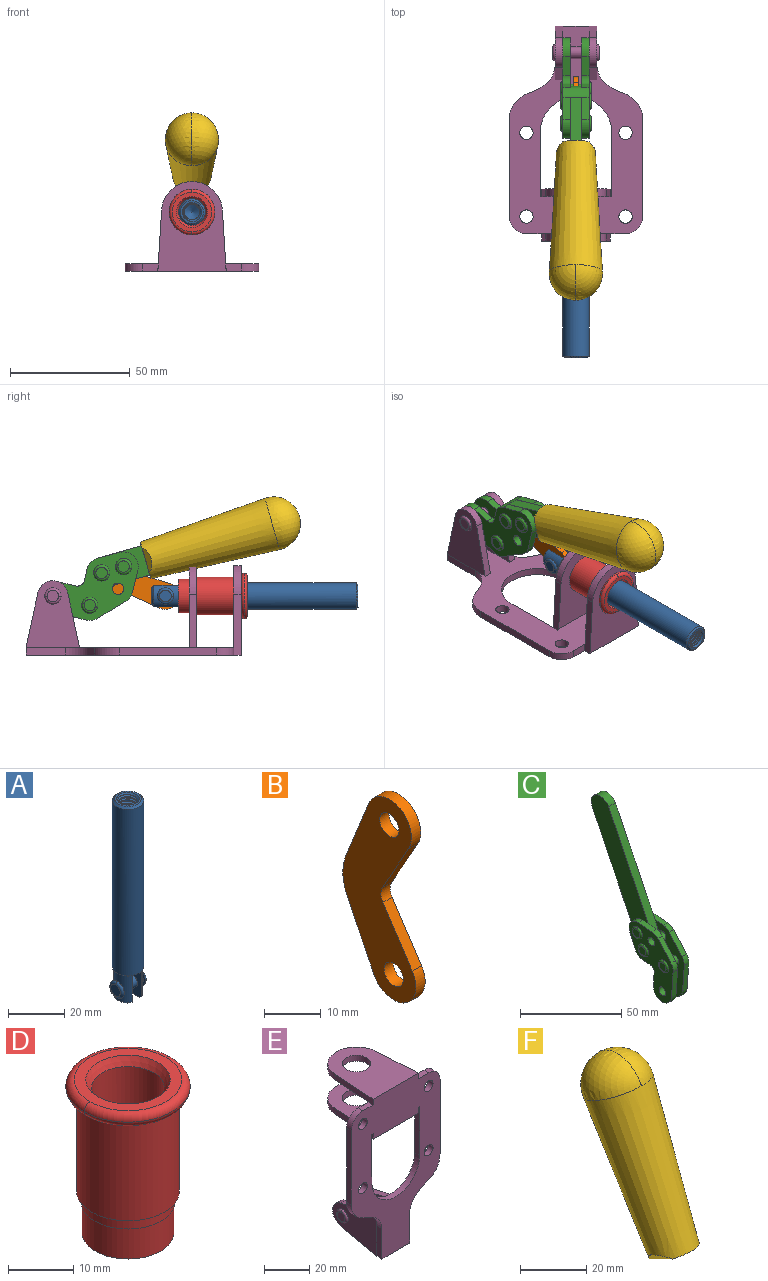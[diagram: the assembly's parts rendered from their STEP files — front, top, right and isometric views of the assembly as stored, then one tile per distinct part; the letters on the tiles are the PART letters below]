
ASSEMBLY  parts=6 mates=6
PART A: 48 faces, bbox 12.6x11.1x86.1 mm
  f0: torus R=2.41mm, axis (-1,0,0), area 15mm2, adj f30,f32,f34
  f1: torus R=2.41mm, axis (-1,0,0), area 15mm2, adj f29,f31,f33
  f2: cylinder r=5.54mm len=72.39mm, axis (0,0,1), area 2518.5mm2, adj f3,f4,f42,f43
  f3: cone r=5.54mm half-angle=45deg, axis (0,0,1), area 7.6mm2, adj f2,f5,f41
  f4: cone r=5.54mm half-angle=45deg, axis (0,0,-1), area 34.9mm2, adj f2,f39
  f5: cylinder r=5.08mm len=11.48mm, axis (0,0,1), area 108.3mm2, adj f3,f7,f8,f41
  f6: cylinder r=2.41mm len=4.83mm, axis (-1,0,0), area 71.2mm2, adj f40,f41
  f7: cylinder r=2.41mm len=4.83mm, axis (-1,0,0), area 7.6mm2, adj f5,f34
  f8: cone r=5.08mm half-angle=45deg, axis (0,0,1), area 10.6mm2, adj f5,f37,f41
  f9: cone r=3.98mm half-angle=45deg, axis (0,0,1), area 17.6mm2, adj f27,f39,f45,f46,f47
  f10: cylinder r=2.41mm len=4.83mm, axis (-1,0,0), area 7.6mm2, adj f33,f38
  f11: cylinder r=3.2mm len=6.4mm, axis (0,0,1), area 78.4mm2, adj f12,f28,f44,f45,f47
  f12: cylinder r=3.2mm len=6.4mm, axis (0,0,1), area 10.5mm2, adj f11,f13,f45,f47
  f13: cylinder r=3.2mm len=6.4mm, axis (0,0,1), area 10.5mm2, adj f12,f14,f45,f47
  f14: cylinder r=3.2mm len=6.4mm, axis (0,0,1), area 10.5mm2, adj f13,f15,f45,f47
  f15: cylinder r=3.2mm len=6.4mm, axis (0,0,1), area 10.5mm2, adj f14,f16,f45,f47
  f16: cylinder r=3.2mm len=6.4mm, axis (0,0,1), area 10.5mm2, adj f15,f17,f45,f47
  f17: cylinder r=3.2mm len=6.4mm, axis (0,0,1), area 10.5mm2, adj f16,f18,f45,f47
  f18: cylinder r=3.2mm len=6.4mm, axis (0,0,1), area 10.5mm2, adj f17,f19,f45,f47
  f19: cylinder r=3.2mm len=6.4mm, axis (0,0,1), area 10.5mm2, adj f18,f20,f45,f47
  f20: cylinder r=3.2mm len=6.4mm, axis (0,0,1), area 10.5mm2, adj f19,f21,f45,f47
  f21: cylinder r=3.2mm len=6.4mm, axis (0,0,1), area 10.5mm2, adj f20,f22,f45,f47
  f22: cylinder r=3.2mm len=6.4mm, axis (0,0,1), area 10.5mm2, adj f21,f23,f45,f47
  f23: cylinder r=3.2mm len=6.4mm, axis (0,0,1), area 10.5mm2, adj f22,f24,f45,f47
  f24: cylinder r=3.2mm len=6.4mm, axis (0,0,1), area 10.5mm2, adj f23,f25,f45,f47
  f25: cylinder r=3.2mm len=6.4mm, axis (0,0,1), area 10.5mm2, adj f24,f26,f45,f47
  f26: cylinder r=3.2mm len=6.4mm, axis (0,0,1), area 10.5mm2, adj f25,f27,f45,f47
  f27: cylinder r=3.2mm len=6.4mm, axis (0,0,1), area 7.4mm2, adj f9,f26,f45,f47
  f28: cone r=3.2mm half-angle=60deg, axis (0,0,1), area 37.2mm2, adj f11
  f29: plane 4.83x4.83mm, normal (-1,0,0), area 18.3mm2, adj f1,f31
  f30: plane 4.83x4.83mm, normal (1,0,0), area 18.3mm2, adj f0,f32
  f31: torus R=2.41mm, axis (-1,0,0), area 15mm2, adj f1,f29,f33
  f32: torus R=2.41mm, axis (-1,0,0), area 15mm2, adj f0,f30,f34
  f33: plane 6.83x6.83mm, normal (1,0,0), area 18.3mm2, adj f1,f10,f31
  f34: plane 6.83x6.83mm, normal (-1,0,0), area 18.3mm2, adj f0,f7,f32
  f35: cone r=5.08mm half-angle=45deg, axis (0,0,1), area 10.6mm2, adj f36,f38,f40
  f36: plane 7.25x1.97mm, normal (0,0,-1), area 10mm2, adj f35,f40
  f37: plane 7.25x1.97mm, normal (0,0,-1), area 10mm2, adj f8,f41
  f38: cylinder r=5.08mm len=11.48mm, axis (0,0,1), area 108.3mm2, adj f10,f35,f40,f42
  f39: plane 9.55x9.55mm, normal (0,0,1), area 22mm2, adj f4,f9
  f40: plane 12.76x10.09mm, normal (1,0,0), area 95.7mm2, adj f6,f35,f36,f38,f42,f43
  f41: plane 12.76x10.09mm, normal (-1,0,0), area 95.7mm2, adj f3,f5,f6,f8,f37,f43
  f42: cone r=5.54mm half-angle=45deg, axis (0,0,1), area 7.6mm2, adj f2,f38,f40
  f43: plane 11.07x4.7mm, normal (0,0,-1), area 50.4mm2, adj f2,f40,f41
  f44: plane 0.89x0.62mm, normal (-1,0,0), area 0.3mm2, adj f11,f45,f46,f47
  f45: bspline ~24.8x7.63mm, area 266.6mm2, adj f9,f11,f12,f13,f14,f15,f16,f17
  f46: bspline ~24.87x7.63mm, area 73.6mm2, adj f9,f44,f45,f47
  f47: bspline ~24.98x7.63mm, area 272.5mm2, adj f9,f11,f12,f13,f14,f15,f16,f17
PART B: 12 faces, bbox 2.3x18.2x42.8 mm
  f0: cylinder r=2.4mm len=4.8mm, axis (1,0,0), area 34.9mm2, adj f4,f11
  f1: cylinder r=10.41mm len=8.47mm, axis (1,0,0), area 20.2mm2, adj f4,f9,f10,f11
  f2: cylinder r=3.05mm len=3.16mm, axis (1,0,0), area 7.7mm2, adj f4,f6,f7,f11
  f3: cylinder r=2.4mm len=4.8mm, axis (1,0,0), area 34.9mm2, adj f4,f11
  f4: plane 42.81x18.23mm, normal (-1,0,0), area 414.1mm2, adj f0,f1,f2,f3,f5,f6,f7,f8
  f5: cylinder r=5.54mm len=10.67mm, axis (1,0,0), area 41.8mm2, adj f4,f6,f10,f11
  f6: plane 11.66x6.53mm, normal (0,-0.87,-0.49), area 30.9mm2, adj f2,f4,f5,f11
  f7: plane 11.17x7.33mm, normal (0,-0.84,0.55), area 30.9mm2, adj f2,f4,f8,f11
  f8: cylinder r=5.54mm len=10.51mm, axis (1,0,0), area 41.8mm2, adj f4,f7,f9,f11
  f9: plane 13.67x6.67mm, normal (0,0.9,-0.44), area 35.1mm2, adj f1,f4,f8,f11
  f10: plane 14.1x5.7mm, normal (0,0.93,0.37), area 35.1mm2, adj f1,f4,f5,f11
  f11: plane 42.81x18.23mm, normal (1,0,0), area 414.1mm2, adj f0,f1,f2,f3,f5,f6,f7,f8
PART C: 59 faces, bbox 12.9x60.2x99.6 mm
  f0: torus R=2.39mm, axis (-1,0,0), area 14.9mm2, adj f20,f43,f51
  f1: torus R=2.39mm, axis (-1,0,0), area 14.9mm2, adj f19,f42,f51
  f2: torus R=2.39mm, axis (-1,0,0), area 14.9mm2, adj f18,f35,f51
  f3: torus R=2.39mm, axis (-1,0,0), area 14.9mm2, adj f14,f17,f23
  f4: torus R=2.39mm, axis (-1,0,0), area 14.9mm2, adj f13,f16,f23
  f5: torus R=2.39mm, axis (-1,0,0), area 14.9mm2, adj f12,f15,f23
  f6: cylinder r=2.39mm len=4.78mm, axis (1,0,0), area 46.5mm2, adj f48,f50,f51
  f7: cylinder r=2.39mm len=4.78mm, axis (1,0,0), area 46.5mm2, adj f50,f51
  f8: cylinder r=6.35mm len=12.68mm, axis (1,0,0), area 61.8mm2, adj f38,f39,f50,f51
  f9: cylinder r=2.39mm len=4.78mm, axis (-1,0,0), area 70.5mm2, adj f46,f50
  f10: cylinder r=2.39mm len=4.78mm, axis (-1,0,0), area 46.5mm2, adj f23,f45,f46
  f11: cylinder r=2.39mm len=4.78mm, axis (-1,0,0), area 46.5mm2, adj f23,f46
  f12: plane 4.78x4.78mm, normal (1,0,0), area 17.9mm2, adj f5,f15
  f13: plane 4.78x4.78mm, normal (1,0,0), area 17.9mm2, adj f4,f16
  f14: plane 4.78x4.78mm, normal (1,0,0), area 17.9mm2, adj f3,f17
  f15: torus R=2.39mm, axis (-1,0,0), area 14.9mm2, adj f5,f12,f23
  f16: torus R=2.39mm, axis (-1,0,0), area 14.9mm2, adj f4,f13,f23
  f17: torus R=2.39mm, axis (-1,0,0), area 14.9mm2, adj f3,f14,f23
  f18: plane 4.78x4.78mm, normal (-1,0,0), area 17.9mm2, adj f2,f35
  f19: plane 4.78x4.78mm, normal (-1,0,0), area 17.9mm2, adj f1,f42
  f20: plane 4.78x4.78mm, normal (-1,0,0), area 17.9mm2, adj f0,f43
  f21: plane 2.26x0.2mm, normal (1,0,0), area 0.2mm2, adj f31,f44
  f22: plane 2.26x0.2mm, normal (-1,0,0), area 0.2mm2, adj f41,f44
  f23: plane 39.37x30.77mm, normal (1,0,0), area 565.5mm2, adj f3,f4,f5,f10,f11,f15,f16,f17
  f24: cylinder r=6.1mm len=4.15mm, axis (-1,0,0), area 14.7mm2, adj f23,f25,f32,f46
  f25: plane 10.25x9.01mm, normal (0,-0.75,0.66), area 42.3mm2, adj f23,f24,f26,f46
  f26: cylinder r=6.35mm len=4.64mm, axis (-1,0,0), area 15.6mm2, adj f23,f25,f27,f46
  f27: plane 15.84x3.1mm, normal (0,-1,-0.07), area 49.2mm2, adj f23,f26,f28,f46
  f28: cylinder r=6.35mm len=12.68mm, axis (-1,0,0), area 61.8mm2, adj f23,f27,f29,f46
  f29: plane 8.11x3.1mm, normal (0,1,0.07), area 25.2mm2, adj f23,f28,f30,f46
  f30: cylinder r=3.05mm len=3.25mm, axis (-1,0,0), area 14.8mm2, adj f23,f29,f31,f46
  f31: plane 5.99x3.1mm, normal (0,0.07,-1), area 18.6mm2, adj f21,f23,f30,f44,f46
  f32: plane 9.5x3.1mm, normal (0,-0.07,1), area 29.5mm2, adj f23,f24,f33,f46,f47
  f33: cylinder r=6.1mm len=8.63mm, axis (-1,0,0), area 39.1mm2, adj f23,f32,f34,f47
  f34: plane 8.65x3.96mm, normal (0,0.91,-0.42), area 29.5mm2, adj f23,f33,f44,f47
  f35: torus R=2.39mm, axis (-1,0,0), area 14.9mm2, adj f2,f18,f51
  f36: plane 10.25x9.01mm, normal (0,-0.75,0.66), area 42.3mm2, adj f37,f49,f50,f51
  f37: cylinder r=6.35mm len=4.64mm, axis (1,0,0), area 15.6mm2, adj f36,f38,f50,f51
  f38: plane 15.84x3.1mm, normal (0,-1,-0.07), area 49.2mm2, adj f8,f37,f50,f51
  f39: plane 8.11x3.1mm, normal (0,1,0.07), area 25.2mm2, adj f8,f40,f50,f51
  f40: cylinder r=3.05mm len=3.25mm, axis (1,0,0), area 14.8mm2, adj f39,f41,f50,f51
  f41: plane 5.99x3.1mm, normal (0,0.07,-1), area 18.6mm2, adj f22,f40,f44,f50,f51
  f42: torus R=2.39mm, axis (-1,0,0), area 14.9mm2, adj f1,f19,f51
  f43: torus R=2.39mm, axis (-1,0,0), area 14.9mm2, adj f0,f20,f51
  f44: cylinder r=6.35mm len=12.12mm, axis (-1,0,0), area 128.9mm2, adj f21,f22,f23,f31,f34,f41,f46,f47
  f45: plane 2.65x1.35mm, normal (1,0,0), area 1mm2, adj f10,f55
  f46: plane 39.08x20.42mm, normal (-1,0,0), area 412.5mm2, adj f9,f10,f11,f24,f25,f26,f27,f28
  f47: plane 77.62x39.82mm, normal (1,0,0), area 850mm2, adj f32,f33,f34,f44,f53,f54,f55
  f48: plane 2.65x1.35mm, normal (-1,0,0), area 1mm2, adj f6,f55
  f49: cylinder r=6.1mm len=4.15mm, axis (1,0,0), area 14.7mm2, adj f36,f50,f51,f56
  f50: plane 39.08x20.42mm, normal (1,0,0), area 412.5mm2, adj f6,f7,f8,f9,f36,f37,f38,f39
  f51: plane 39.37x30.77mm, normal (-1,0,0), area 565.5mm2, adj f0,f1,f2,f6,f7,f8,f35,f36
  f52: plane 8.65x3.96mm, normal (0,0.91,-0.42), area 29.5mm2, adj f44,f51,f57,f58
  f53: plane 68.49x33.4mm, normal (0,0.9,-0.44), area 358.1mm2, adj f44,f47,f54,f58
  f54: cylinder r=6.35mm len=12.06mm, axis (1,0,0), area 93.7mm2, adj f47,f53,f55,f58
  f55: plane 68.49x33.4mm, normal (0,-0.9,0.44), area 358.1mm2, adj f44,f45,f46,f47,f48,f50,f54,f58
  f56: plane 9.5x3.1mm, normal (0,-0.07,1), area 29.5mm2, adj f49,f50,f51,f57,f58
  f57: cylinder r=6.1mm len=8.63mm, axis (1,0,0), area 39.1mm2, adj f51,f52,f56,f58
  f58: plane 77.62x39.82mm, normal (-1,0,0), area 850mm2, adj f44,f52,f53,f54,f55,f56,f57
PART D: 15 faces, bbox 20.6x20.6x28.7 mm
  f0: torus R=8.26mm, axis (0,0,1), area 56.8mm2, adj f1,f10,f12
  f1: torus R=8.26mm, axis (0,0,1), area 56.8mm2, adj f0,f6,f13
  f2: cylinder r=5.59mm len=25.91mm, axis (0,0,1), area 909.6mm2, adj f3,f4
  f3: cone r=6.86mm half-angle=45deg, axis (0,0,-1), area 70.2mm2, adj f2,f14
  f4: cone r=6.47mm half-angle=30deg, axis (0,0,1), area 66.7mm2, adj f2,f13
  f5: cylinder r=7.04mm len=14.07mm, axis (0,0,1), area 252.6mm2, adj f11,f14
  f6: torus R=8.26mm, axis (0,0,1), area 56.8mm2, adj f1,f12,f13
  f7: cylinder r=7.16mm len=14.33mm, axis (0,0,1), area 91.5mm2, adj f9,f11
  f8: cylinder r=7.86mm len=18.42mm, axis (0,0,1), area 909.6mm2, adj f9,f10
  f9: plane 15.72x15.72mm, normal (0,0,-1), area 33mm2, adj f7,f8
  f10: plane 16.51x16.51mm, normal (0,0,-1), area 19.9mm2, adj f0,f8,f12
  f11: plane 14.33x14.33mm, normal (0,0,-1), area 5.7mm2, adj f5,f7
  f12: torus R=8.26mm, axis (0,0,1), area 56.8mm2, adj f0,f6,f10
  f13: plane 16.51x16.51mm, normal (0,0,1), area 82.7mm2, adj f1,f4,f6
  f14: plane 14.07x14.07mm, normal (0,0,-1), area 7.8mm2, adj f3,f5
PART E: 55 faces, bbox 55.7x37.4x89.8 mm
  f0: torus R=2.41mm, axis (-1,0,0), area 15mm2, adj f11,f15,f25
  f1: torus R=2.41mm, axis (-1,0,0), area 15mm2, adj f10,f12,f22
  f2: cylinder r=2.78mm len=5.56mm, axis (0,-1,0), area 54.2mm2, adj f30,f54
  f3: cylinder r=14.99mm len=29.97mm, axis (0,-1,0), area 145.9mm2, adj f30,f49,f53,f54
  f4: cylinder r=2.78mm len=5.56mm, axis (0,-1,0), area 54.2mm2, adj f30,f54
  f5: cylinder r=2.78mm len=5.56mm, axis (0,-1,0), area 54.2mm2, adj f30,f54
  f6: cylinder r=2.78mm len=5.56mm, axis (0,-1,0), area 54.2mm2, adj f30,f54
  f7: cylinder r=6.35mm len=12.7mm, axis (0,0,1), area 123.6mm2, adj f27,f51
  f8: cylinder r=6.35mm len=12.7mm, axis (0,0,-1), area 124.7mm2, adj f21,f35
  f9: cylinder r=2.41mm len=11.18mm, axis (-1,0,0), area 169.4mm2, adj f16,f19
  f10: plane 4.83x4.83mm, normal (1,0,0), area 18.3mm2, adj f1,f12
  f11: plane 4.83x4.83mm, normal (-1,0,0), area 18.3mm2, adj f0,f15
  f12: torus R=2.41mm, axis (-1,0,0), area 15mm2, adj f1,f10,f22
  f13: cylinder r=6.35mm len=12.41mm, axis (1,0,0), area 53.4mm2, adj f18,f19,f22,f23
  f14: cylinder r=6.35mm len=12.41mm, axis (-1,0,0), area 53.4mm2, adj f16,f17,f24,f25
  f15: torus R=2.41mm, axis (-1,0,0), area 15mm2, adj f0,f11,f25
  f16: plane 27.86x22.35mm, normal (1,0,0), area 425.4mm2, adj f9,f14,f17,f24,f30
  f17: plane 22.86x4.97mm, normal (0,0.21,0.98), area 72.5mm2, adj f14,f16,f25,f30
  f18: plane 22.86x4.97mm, normal (0,0.21,0.98), area 72.5mm2, adj f13,f19,f22,f30
  f19: plane 27.86x22.35mm, normal (-1,0,0), area 425.4mm2, adj f9,f13,f18,f23,f30
  f20: cylinder r=12.7mm len=25.35mm, axis (0,0,-1), area 119.8mm2, adj f21,f34,f35,f36
  f21: plane 34.21x28.07mm, normal (0,0,-1), area 702.4mm2, adj f8,f20,f30,f34,f36
  f22: plane 27.96x22.45mm, normal (1,0,0), area 407.2mm2, adj f1,f12,f13,f18,f23,f30,f42,f43
  f23: plane 22.86x4.97mm, normal (0,0.21,-0.98), area 72.5mm2, adj f13,f19,f22,f44
  f24: plane 22.86x4.97mm, normal (0,0.21,-0.98), area 72.5mm2, adj f14,f16,f25,f44
  f25: plane 27.86x22.35mm, normal (-1,0,0), area 407.1mm2, adj f0,f14,f15,f17,f24,f30,f45,f46
  f26: plane 3.1x0.95mm, normal (0,0,-1), area 2.7mm2, adj f30,f49,f50,f54
  f27: plane 34.21x28.07mm, normal (0,0,1), area 702.4mm2, adj f7,f28,f30,f50,f52
  f28: cylinder r=12.7mm len=25.35mm, axis (0,0,1), area 118.8mm2, adj f27,f50,f51,f52
  f29: plane 3.1x0.95mm, normal (0,0,-1), area 2.7mm2, adj f30,f52,f53,f54
  f30: plane 86.54x55.63mm, normal (0,1,0), area 2362.9mm2, adj f2,f3,f4,f5,f6,f16,f17,f18
  f31: plane 40.56x3.1mm, normal (-1,0,0), area 125.7mm2, adj f30,f32,f48,f54
  f32: cylinder r=7.11mm len=7.11mm, axis (0,-1,0), area 34.6mm2, adj f30,f31,f33,f54
  f33: plane 6.67x3.1mm, normal (0,0,1), area 20.4mm2, adj f30,f32,f34,f54
  f34: plane 25.39x3.13mm, normal (-1,0.06,0), area 79.5mm2, adj f20,f21,f33,f35,f54
  f35: plane 37.31x28.45mm, normal (0,0,1), area 789.9mm2, adj f8,f20,f34,f36,f54
  f36: plane 25.39x3.13mm, normal (1,0.06,0), area 79.5mm2, adj f20,f21,f35,f37,f54
  f37: plane 6.67x3.1mm, normal (0,0,1), area 20.4mm2, adj f30,f36,f38,f54
  f38: cylinder r=7.11mm len=7.11mm, axis (0,-1,0), area 34.6mm2, adj f30,f37,f39,f54
  f39: plane 40.56x3.1mm, normal (1,0,0), area 125.7mm2, adj f30,f38,f40,f54
  f40: cylinder r=11.18mm len=10.16mm, axis (0,-1,0), area 39.5mm2, adj f30,f39,f41,f54
  f41: plane 6.09x3.1mm, normal (0.42,0,-0.91), area 20.8mm2, adj f30,f40,f42,f54
  f42: cylinder r=11.18mm len=9.41mm, axis (0,-1,0), area 37.2mm2, adj f22,f30,f41,f43,f54
  f43: plane 16.5x3.1mm, normal (1,0,0), area 51.1mm2, adj f22,f42,f44,f54
  f44: plane 17.37x3.1mm, normal (0,0,-1), area 53.8mm2, adj f23,f24,f30,f43,f45,f54
  f45: plane 16.5x3.1mm, normal (-1,0,0), area 51.1mm2, adj f25,f44,f46,f54
  f46: cylinder r=11.18mm len=9.41mm, axis (0,-1,0), area 37.2mm2, adj f25,f30,f45,f47,f54
  f47: plane 6.09x3.1mm, normal (-0.42,0,-0.91), area 20.8mm2, adj f30,f46,f48,f54
  f48: cylinder r=11.18mm len=10.16mm, axis (0,-1,0), area 39.5mm2, adj f30,f31,f47,f54
  f49: plane 26.54x3.1mm, normal (-1,0,0), area 82.3mm2, adj f3,f26,f30,f54
  f50: plane 25.39x3.1mm, normal (1,0.06,0), area 78.8mm2, adj f26,f27,f28,f51,f54
  f51: plane 37.31x28.45mm, normal (0,0,-1), area 789.9mm2, adj f7,f28,f50,f52,f54
  f52: plane 25.39x3.1mm, normal (-1,0.06,0), area 78.8mm2, adj f27,f28,f29,f51,f54
  f53: plane 26.54x3.1mm, normal (1,0,0), area 82.3mm2, adj f3,f29,f30,f54
  f54: plane 89.66x55.63mm, normal (0,-1,0), area 2678.5mm2, adj f2,f3,f4,f5,f6,f26,f29,f31
PART F: 11 faces, bbox 22.3x42.6x64.5 mm
  f0: sphere r=11.13mm, area 411.4mm2, adj f1,f8
  f1: cone r=11.11mm half-angle=3.3deg, axis (0,0.44,0.9), area 3251.8mm2, adj f0,f7,f8,f9,f10
  f2: cylinder r=6.16mm len=11.7mm, axis (1,0,0), area 89.5mm2, adj f3,f4,f5,f6
  f3: plane 60.23x36.75mm, normal (-1,0,0), area 763.6mm2, adj f2,f4,f6,f10
  f4: plane 51.37x25.05mm, normal (0,0.9,-0.44), area 264.2mm2, adj f2,f3,f5,f10
  f5: plane 60.23x36.75mm, normal (1,0,0), area 763.6mm2, adj f2,f4,f6,f10
  f6: plane 51.37x25.05mm, normal (0,-0.9,0.44), area 264.2mm2, adj f2,f3,f5,f10
  f7: plane 9.95x5.95mm, normal (0.71,-0.31,-0.64), area 25.8mm2, adj f1,f10
  f8: sphere r=11.13mm, area 411.4mm2, adj f0,f1
  f9: plane 9.95x5.95mm, normal (-0.71,-0.31,-0.64), area 25.8mm2, adj f1,f10
  f10: plane 14.27x11.38mm, normal (0,-0.44,-0.9), area 106.7mm2, adj f1,f3,f4,f5,f6,f7,f9
PLACE A rot(axis=(1,0,0),90deg) t=(0,9.79,0)mm
PLACE B rot(axis=(1,0,0),85.1deg) t=(0,7.61,-1.24)mm
PLACE C rot(axis=(1,0,0),100deg) t=(0,13.9,-5.2)mm
PLACE D rot(axis=(0.58,0.58,-0.58),120deg) t=(-24.61,9.14,24.61)mm
PLACE E rot(axis=(1,0,0),90deg) t=(0,9.14,0)mm fixed
PLACE F rot(axis=(1,0,0),100deg) t=(-0.04,13.9,-5.2)mm
MATE revolute B.f5 <-> A.f6  axis (1,0,0) through (0,-5.69,24.61)mm
MATE fastened D.f2 <-> E.f7  axis (0,-1,0) through (0,-37.25,24.61)mm
MATE fastened C.f54 <-> F.f2  axis (-1,0,0) through (-2.35,-52.38,55.25)mm
MATE revolute C.f7 <-> E.f0  axis (-1,0,0) through (0,41.23,24.61)mm
MATE slider A.f2 <-> D.f2  axis (0,-1,0) through (0,-48.99,24.61)mm
MATE revolute B.f3 <-> C.f4  axis (1,0,0) through (0,25.83,20.77)mm
